# Revit family: Roof_Drain-Jay R. Smith-Round_Type-1920_Series
name_source: partatom
category: Plumbing Fixtures
units: mm (PartAtom-declared; Revit-internal decimal feet)

## family parameters
Always vertical = Yes
Cut with Voids When Loaded = No
OmniClass Number = 23.70.50.21.24.11
OmniClass Title = Roof Waste Water Drains
Part Type = Normal
Room Calculation Point = No
Round Connector Dimension = Use Diameter
Shared = No
Work Plane-Based = Yes

## types (15) — shared parameters
Assembly Code = D2040200
C - Underdeck Clamp = No
C2 - Secondary Flashing Clamp = No
CW Connection = No
Default Elevation = 0"
Description = Plaza and Planter Drain
Diameter = 12"
Dome Height = 4 1/2"
Finish = Cast Iron-Jay R Smith-Duco Coated
G - Galvanized Cast Iron = No
HW Connection = No
Installation Type = Roof Mounted
L - Speedi-Set Service Weight - 02"(50), 03"(75) & 04"(100) sizes only = No
LXH - Speedi-Set Extra Heavy - 02"(50), 03"(75) & 04"(100) sizes only = No
M - Ductile Iron Grate = No
Manufacturer = Jay R. Smith Mfg. Co.
Material = Cast Iron-Jay R Smith-Duco Coated
Mesh Material = Stainless Steel-Jay R Smith-Mesh
NB - Nickel Bronze Top = No
PB - Polished Bronze Top = No
R - Sump Receiver = No
SSP - Stainless Steel Standpipe = No
SSP4 - 4" Dia. Stainless Steel Standpipe = No
Stainless Steel Mesh Screen Over Perforated Standpipe = No
Standpipe Material = PVC-Jay R Smith-Perforated
U - Vandal Proof Dome = No
URL = http://www.jrsmith.com
Upper Drain As Specified = No
Vent Connection = No
Waste Connection = Yes

## per-type parameters (varying)
| type | B Dimension | Connection Outlet Description | Connection Radius | Connection Size | T - Threaded Outlet |
| 1920Y02 | 6" | 2" No-HUB Outlet Connection | 1" | 2" | No |
| 1920Y03 | 6" | 3" No-HUB Outlet Connection | 1 1/2" | 3" | No |
| 1920Y04 | 6" | 4" No-HUB Outlet Connection | 2" | 4" | No |
| 1920Y05 | 6" | 5" No-HUB Outlet Connection | 2 1/2" | 5" | No |
| 1920Y06 | 6" | 6" No-HUB Outlet Connection | 3" | 6" | No |
| 1920C02 | 6" | 2" Caulk Outlet Connection | 1" | 2" | No |
| 1920C03 | 6" | 3" Caulk Outlet Connection | 1 1/2" | 3" | No |
| 1920C04 | 6" | 4" Caulk Outlet Connection | 2" | 4" | No |
| 1920C05 | 6" | 5" Caulk Outlet Connection | 2 1/2" | 5" | No |
| 1920C06 | 6" | 6" Caulk Outlet Connection | 3" | 6" | No |
| 1920T02 | 4 3/4" | 2" Threaded Outlet Connection | 1" | 2" | Yes |
| 1920T03 | 4 3/4" | 3" Threaded Outlet Connection | 1 1/2" | 3" | Yes |
| 1920T04 | 4 3/4" | 4" Threaded Outlet Connection | 2" | 4" | Yes |
| 1920T05 | 4 3/4" | 5" Threaded Outlet Connection | 2 1/2" | 5" | Yes |
| 1920T06 | 4 3/4" | 6" Threaded Outlet Connection | 3" | 6" | Yes |

note: column(s) folded — value = type name in every type: Model

## geometry (parser evidence)
native form markers: Sweep x6
no freeform markers — native parametric forms only
